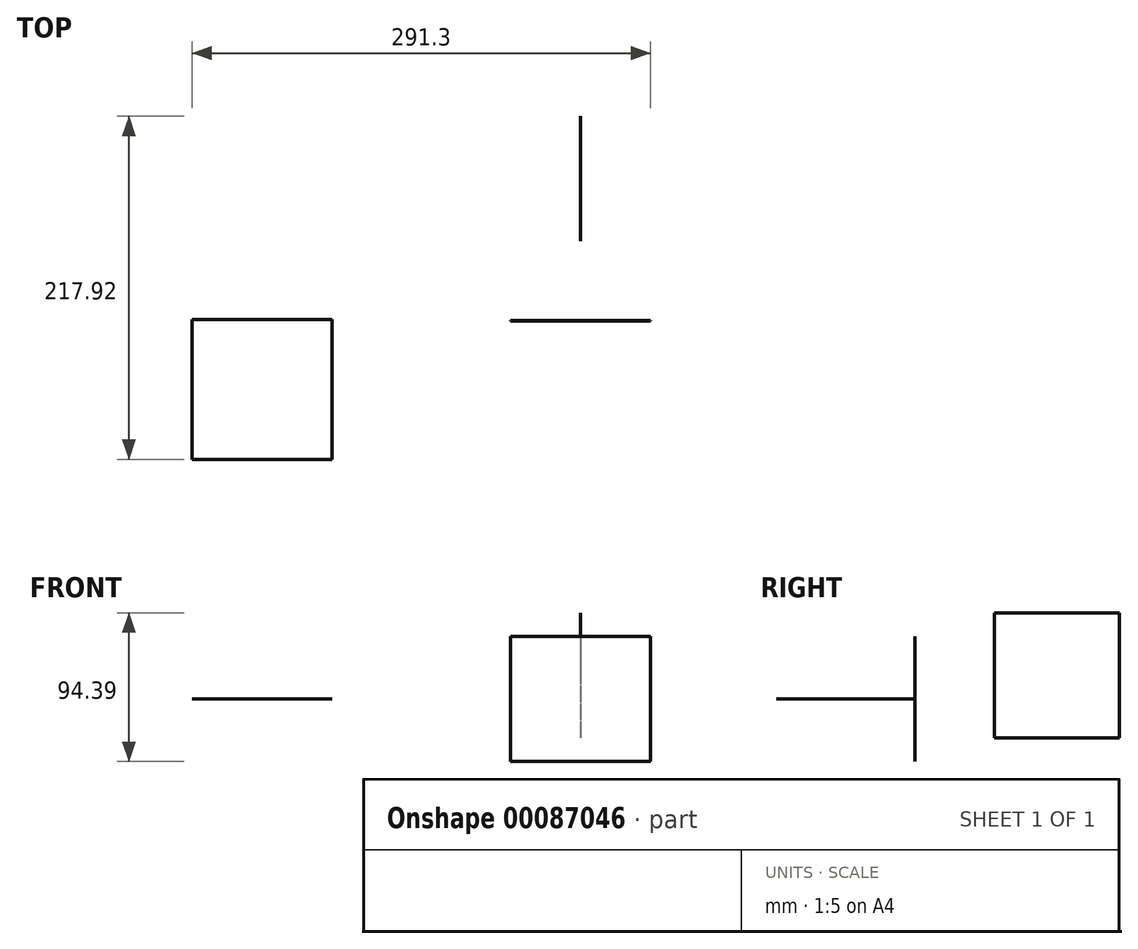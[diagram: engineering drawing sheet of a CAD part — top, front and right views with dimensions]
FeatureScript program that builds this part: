
annotation { "Feature Type Name" : "Feature", "Feature Type Description" : "" }
export const myFeature = defineFeature(function(context is Context, id is Id, definition is map)
    precondition{}
    {
        {
            assignVariable(context, id + "F0", {"name" : "thickness", "anyValue" : 3 / 16});
        }
        {
            var Q0;
            Q0=qCreatedBy(makeId("Front.planeOp"),FACE);
            var sketch = newSketch(context, id + "F1", { "sketchPlane" : qUnion([Q0])});
            skLineSegment(sketch, "E0.bottom", {"start": v(44.45, 39.69) * mm, "end": v(-44.45, 39.69) * mm});
            skLineSegment(sketch, "E0.top", {"start": v(44.45, -39.69) * mm, "end": v(-44.45, -39.69) * mm});
            skLineSegment(sketch, "E0.left", {"start": v(44.45, 39.69) * mm, "end": v(44.45, -39.69) * mm});
            skLineSegment(sketch, "E0.right", {"start": v(-44.45, 39.69) * mm, "end": v(-44.45, -39.69) * mm});
            skPoint(sketch, "E0.middle", {"position": v(0, 0) * mm});
            skSolve(sketch);
        }
        {
            var Q0;
            Q0=makeQuery(id+"F1.imprint","IMPRINT",FACE,{"disambiguationData":[TD([[makeQuery(id+"F1.imprint","IMPRINT",EDGE,{"derivedFrom":sQuery(id+"F1.wireOp",EDGE,"E0.bottom")}),1.0]])]});
            extrude(context, id + "F2", {"entities" : qUnion([Q0]), "endBound" : BoundingType.SYMMETRIC, "depth" : (getVariable(context, 'thickness')) * mm});
        }
        {
            var Q0;
            Q0=qCreatedBy(makeId("Right.planeOp"),FACE);
            var sketch = newSketch(context, id + "F3", { "sketchPlane" : qUnion([Q0])});
            skLineSegment(sketch, "E1.bottom", {"start": v(50.6, 54.7) * mm, "end": v(129.97, 54.7) * mm});
            skLineSegment(sketch, "E1.top", {"start": v(50.6, -24.68) * mm, "end": v(129.97, -24.68) * mm});
            skLineSegment(sketch, "E1.left", {"start": v(50.6, 54.7) * mm, "end": v(50.6, -24.68) * mm});
            skLineSegment(sketch, "E1.right", {"start": v(129.97, 54.7) * mm, "end": v(129.97, -24.68) * mm});
            skSolve(sketch);
        }
        {
            var Q0;
            Q0=makeQuery(id+"F3.imprint","IMPRINT",FACE,{"disambiguationData":[TD([[makeQuery(id+"F3.imprint","IMPRINT",EDGE,{"derivedFrom":sQuery(id+"F3.wireOp",EDGE,"E1.bottom")}),-1.0]])]});
            extrude(context, id + "F4", {"entities" : qUnion([Q0]), "endBound" : BoundingType.SYMMETRIC, "depth" : (getVariable(context, 'thickness')) * mm});
        }
        {
            var Q0;
            Q0=qCreatedBy(makeId("Top.planeOp"),FACE);
            var sketch = newSketch(context, id + "F5", { "sketchPlane" : qUnion([Q0])});
            skLineSegment(sketch, "E2.bottom", {"start": v(-246.85, -87.95) * mm, "end": v(-157.95, -87.95) * mm});
            skLineSegment(sketch, "E2.top", {"start": v(-246.85, 0.95) * mm, "end": v(-157.95, 0.95) * mm});
            skLineSegment(sketch, "E2.left", {"start": v(-246.85, -87.95) * mm, "end": v(-246.85, 0.95) * mm});
            skLineSegment(sketch, "E2.right", {"start": v(-157.95, -87.95) * mm, "end": v(-157.95, 0.95) * mm});
            skSolve(sketch);
        }
        {
            var Q0;
            Q0=makeQuery(id+"F5.imprint","IMPRINT",FACE,{"disambiguationData":[TD([[makeQuery(id+"F5.imprint","IMPRINT",EDGE,{"derivedFrom":sQuery(id+"F5.wireOp",EDGE,"E2.bottom")}),1.0]])]});
            extrude(context, id + "F6", {"entities" : qUnion([Q0]), "endBound" : BoundingType.SYMMETRIC, "depth" : (getVariable(context, 'thickness')) * mm});
        }
    });
